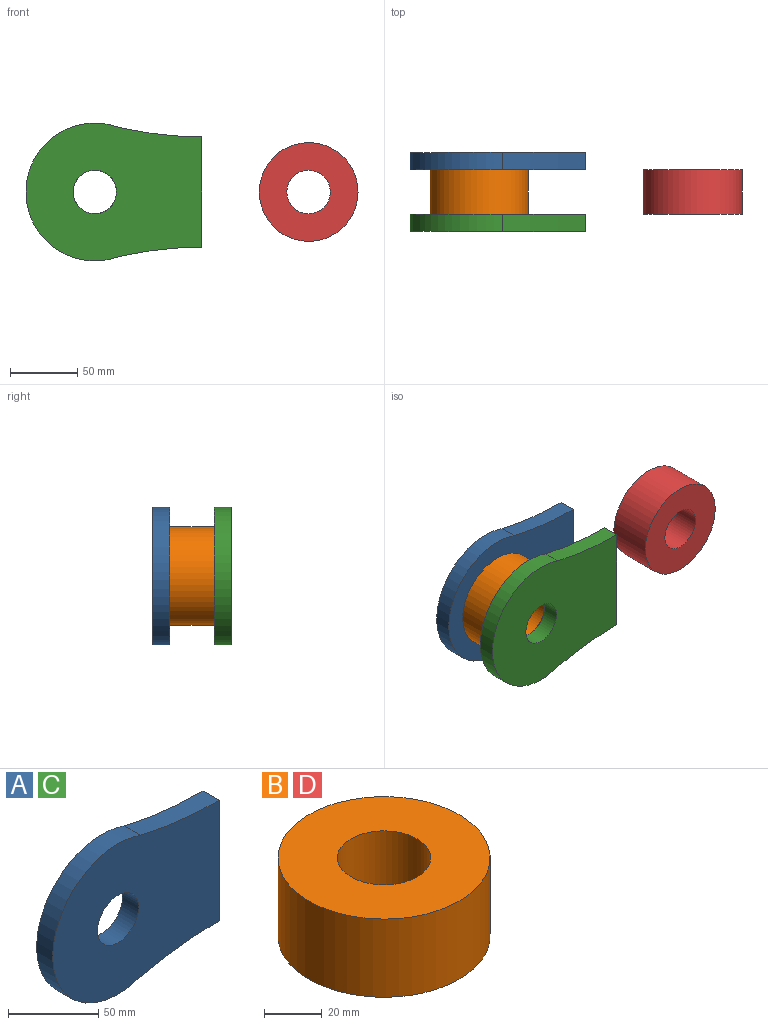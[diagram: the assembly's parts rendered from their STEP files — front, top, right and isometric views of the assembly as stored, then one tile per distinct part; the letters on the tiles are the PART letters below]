
ASSEMBLY  parts=4 mates=2
PART A: 7 faces, bbox 130.4x12.7x102.2 mm
  f0: cylinder r=270.28mm len=61.79mm, axis (0,1,0), area 791.7mm2, adj f2,f3,f4,f6
  f1: cylinder r=270.28mm len=61.79mm, axis (0,1,0), area 791.7mm2, adj f2,f3,f4,f6
  f2: plane 130.36x102.18mm, normal (0,-1,0), area 10377.5mm2, adj f0,f1,f4,f5,f6
  f3: plane 130.36x102.18mm, normal (0,1,0), area 10377.5mm2, adj f0,f1,f4,f5,f6
  f4: cylinder r=51.09mm len=102.18mm, axis (0,1,0), area 2491.5mm2, adj f0,f1,f2,f3
  f5: cylinder r=16.11mm len=32.21mm, axis (0,-1,0), area 1285.3mm2, adj f2,f3
  f6: plane 81.71x12.7mm, normal (1,0,0), area 1037.7mm2, adj f0,f1,f2,f3
PART B: 4 faces, bbox 73.2x73.2x33 mm
  f0: cylinder r=16.11mm len=33.02mm, axis (0,0,-1), area 3341.7mm2, adj f2,f3
  f1: cylinder r=36.58mm len=73.16mm, axis (0,0,-1), area 7588.9mm2, adj f2,f3
  f2: plane 73.16x73.16mm, normal (0,0,1), area 3388.3mm2, adj f0,f1
  f3: plane 73.16x73.16mm, normal (0,0,-1), area 3388.3mm2, adj f0,f1
PART C: same geometry as A
PART D: same geometry as B
PLACE A t=(-29.59,-11.15,-0.63)mm
PLACE B rot(axis=(1,0,0),90deg) t=(-108.85,-23.85,-0.63)mm
PLACE C rot(axis=(1,0,0),180deg) t=(-29.59,-69.57,-0.63)mm
PLACE D rot(axis=(-1,0,0),90deg) t=(49.68,-56.87,-0.63)mm
MATE fastened C.f4 <-> B.f0  axis (0,1,0) through (-108.85,-56.87,-0.63)mm
MATE fastened D.f0 <-> A.f2  axis (0,1,0) through (49.68,-23.85,-0.63)mm
